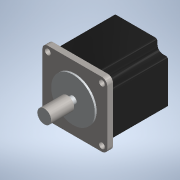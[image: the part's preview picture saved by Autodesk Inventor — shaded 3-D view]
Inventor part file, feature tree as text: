
AUTODESK INVENTOR PART (.ipt)
format: ipt  version: 2020 (Build 240168000, 168)  size: 176,640 bytes
history: mixed  units: mm (DEFAULTED — no unit token found)
features: other x3, direct_edit x2, move_body x2, extrude x1, sketch x1, imported_body x1
ambient origin geometry x8: Origin, YZ Plane, XZ Plane, XY Plane, X Axis, Y Axis, Z Axis, Center Point
bodies: Solid1 (imported_parasolid), Solid2 (imported_parasolid)
feature tree (10):
  other  "NEMA23.SLDPRT"
  direct_edit  "Direct Edit1"
  direct_edit  "Direct Edit2"
  extrude  "Extrusion1"  TaperAngle=0.0deg  [1 undecoded]
  sketch  "Sketch1"  dims[d0=0.0mm d1=0.0mm d2=4.0mm d3=0.0mm d4=0.0mm d5=-1.0mm d6=12.0mm d7=20.0mm d8=0.0mm]
  other  "Boss-Extrude3"
  other  "Boss-Extrude4"
  move_body  "Move1"
  move_body  "Move2"
  imported_body  NMx_Import_Brep_tag  [imported B-rep: ~46 faces, bbox_mm=[56.4, 56.4, 79.6]]
note: 1 required parameter value undecoded (feature->parameter linkage not recoverable at this tier; creation-order binding heuristic only, values carry confidence <= 0.55)
